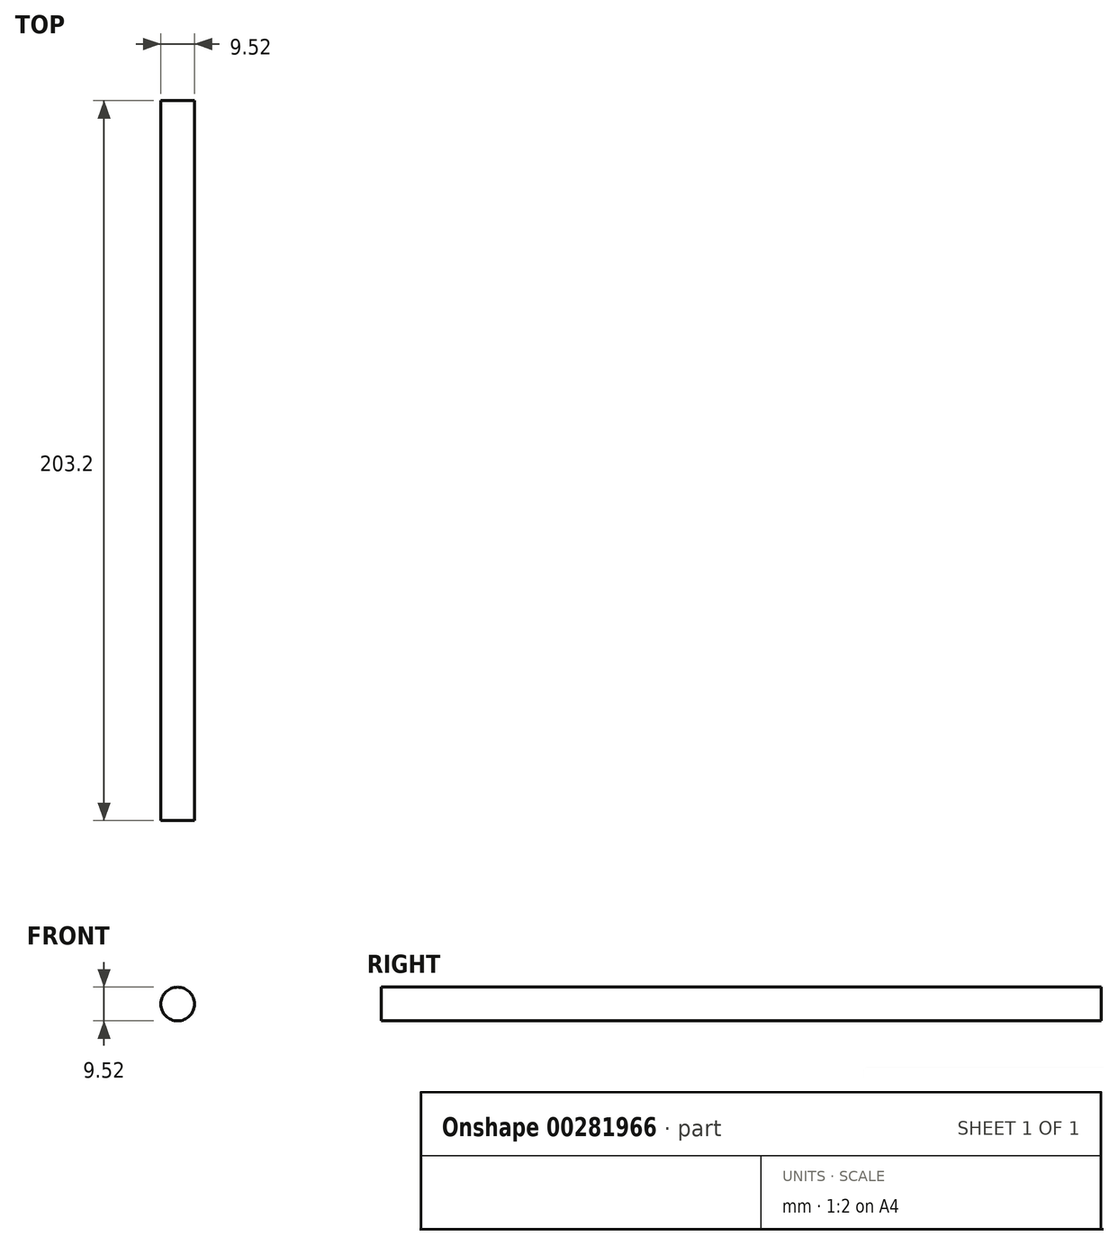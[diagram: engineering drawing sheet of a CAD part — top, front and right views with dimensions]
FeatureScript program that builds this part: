
annotation { "Feature Type Name" : "Feature", "Feature Type Description" : "" }
export const myFeature = defineFeature(function(context is Context, id is Id, definition is map)
    precondition{}
    {
        {
            var Q0;
            Q0=qCreatedBy(makeId("Front.planeOp"),FACE);
            var sketch = newSketch(context, id + "F0", { "sketchPlane" : qUnion([Q0])});
            skCircle(sketch, "E0", {"center": v(-64.35, 37.62) * mm, "radius": 4.76 * mm});
            skSolve(sketch);
        }
        {
            var Q0;
            Q0 = qSketchRegion(id + "F0", true);
            extrude(context, id + "F1", {"entities" : qUnion([Q0]), "depth" : 203.2 * mm});
        }
    });
